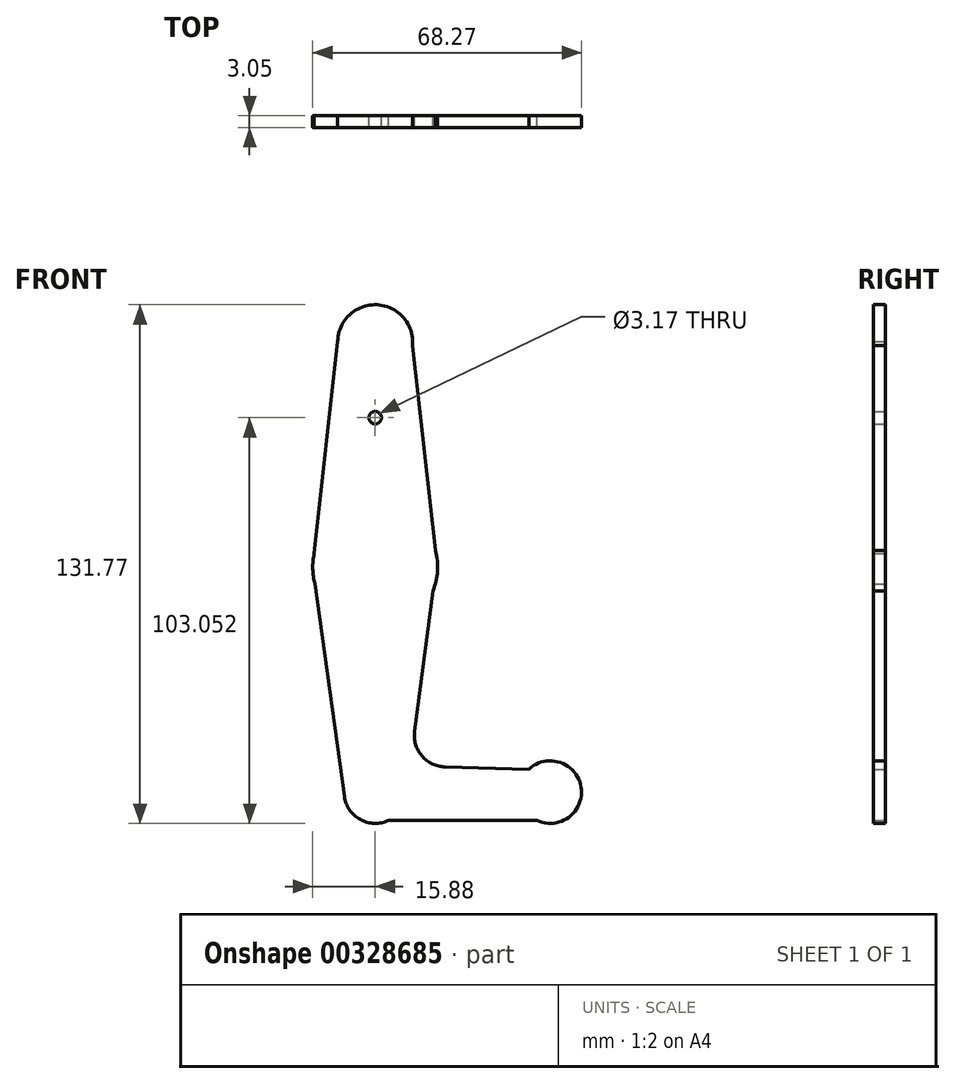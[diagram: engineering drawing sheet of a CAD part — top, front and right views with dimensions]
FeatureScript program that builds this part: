
annotation { "Feature Type Name" : "Feature", "Feature Type Description" : "" }
export const myFeature = defineFeature(function(context is Context, id is Id, definition is map)
    precondition{}
    {
        {
            var Q0;
            Q0=qCreatedBy(makeId("Front.planeOp"),FACE);
            var sketch = newSketch(context, id + "F0", { "sketchPlane" : qUnion([Q0])});
            skLineSegment(sketch, "E0", {"start": v(0, 0) * mm, "end": v(0, 114.3) * mm, "construction": true});
            skLineSegment(sketch, "E1", {"start": v(0, 0) * mm, "end": v(44.45, 0) * mm, "construction": true});
            skCircle(sketch, "E2", {"center": v(0, 114.3) * mm, "radius": 9.53 * mm});
            skCircle(sketch, "E3", {"center": v(0, 57.15) * mm, "radius": 15.88 * mm});
            skCircle(sketch, "E4", {"center": v(0, 0) * mm, "radius": 7.94 * mm});
            skCircle(sketch, "E5", {"center": v(44.45, 0) * mm, "radius": 7.94 * mm});
            skLineSegment(sketch, "E6", {"start": v(39.05, 5.82) * mm, "end": v(17.68, 6.4) * mm});
            skLineSegment(sketch, "E7", {"start": v(3.4, -7.17) * mm, "end": v(41.05, -7.17) * mm});
            skLineSegment(sketch, "E8", {"start": v(15.3, 61.36) * mm, "end": v(9.48, 113.43) * mm});
            skLineSegment(sketch, "E9", {"start": v(-9.52, 114.42) * mm, "end": v(-15.88, 57.15) * mm});
            skLineSegment(sketch, "E10", {"start": v(-15.87, 57.15) * mm, "end": v(-7.86, -1.08) * mm});
            skLineSegment(sketch, "E11", {"start": v(15.73, 59.25) * mm, "end": v(10.01, 15.38) * mm});
            skArc(sketch, "E12.filletArc", {"start": v(10.01, 15.38) * mm, "mid": v(11.85, 9.2) * mm, "end": v(17.68, 6.4) * mm});
            skCircle(sketch, "E13", {"center": v(0, 95.11) * mm, "radius": 1.59 * mm});
            skSolve(sketch);
        }
        {
            var Q0;
            Q0 = qSketchRegion(id + "F0", true);
            extrude(context, id + "F1", {"entities" : qUnion([Q0]), "depth" : 3.05 * mm});
        }
    });
